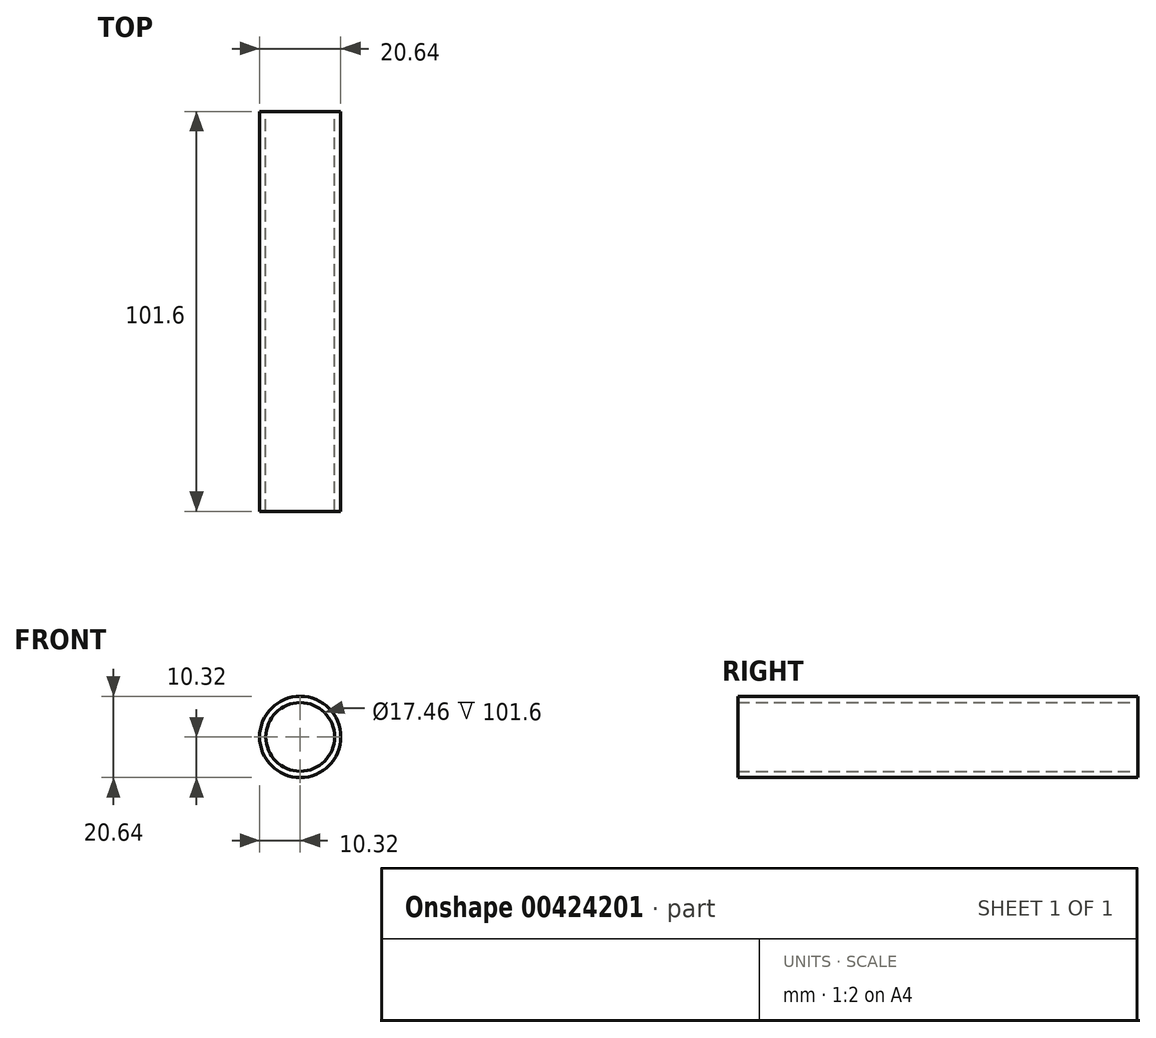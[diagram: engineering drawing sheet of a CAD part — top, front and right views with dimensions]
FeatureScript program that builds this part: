
annotation { "Feature Type Name" : "Feature", "Feature Type Description" : "" }
export const myFeature = defineFeature(function(context is Context, id is Id, definition is map)
    precondition{}
    {
        {
            var Q0;
            Q0=qCreatedBy(makeId("Front.planeOp"),FACE);
            var sketch = newSketch(context, id + "F0", { "sketchPlane" : qUnion([Q0])});
            skCircle(sketch, "E0", {"center": v(0, 0) * mm, "radius": 10.32 * mm});
            skCircle(sketch, "E1", {"center": v(0, 0) * mm, "radius": 8.73 * mm});
            skSolve(sketch);
        }
        {
            var Q0;
            Q0=makeQuery(id+"F0.imprint","IMPRINT",FACE,{"disambiguationData":[TD([[makeQuery(id+"F0.imprint","IMPRINT",EDGE,{"derivedFrom":sQuery(id+"F0.wireOp",EDGE,"E0")}),1.0]])]});
            extrude(context, id + "F1", {"entities" : qUnion([Q0]), "depth" : 101.6 * mm});
        }
    });
